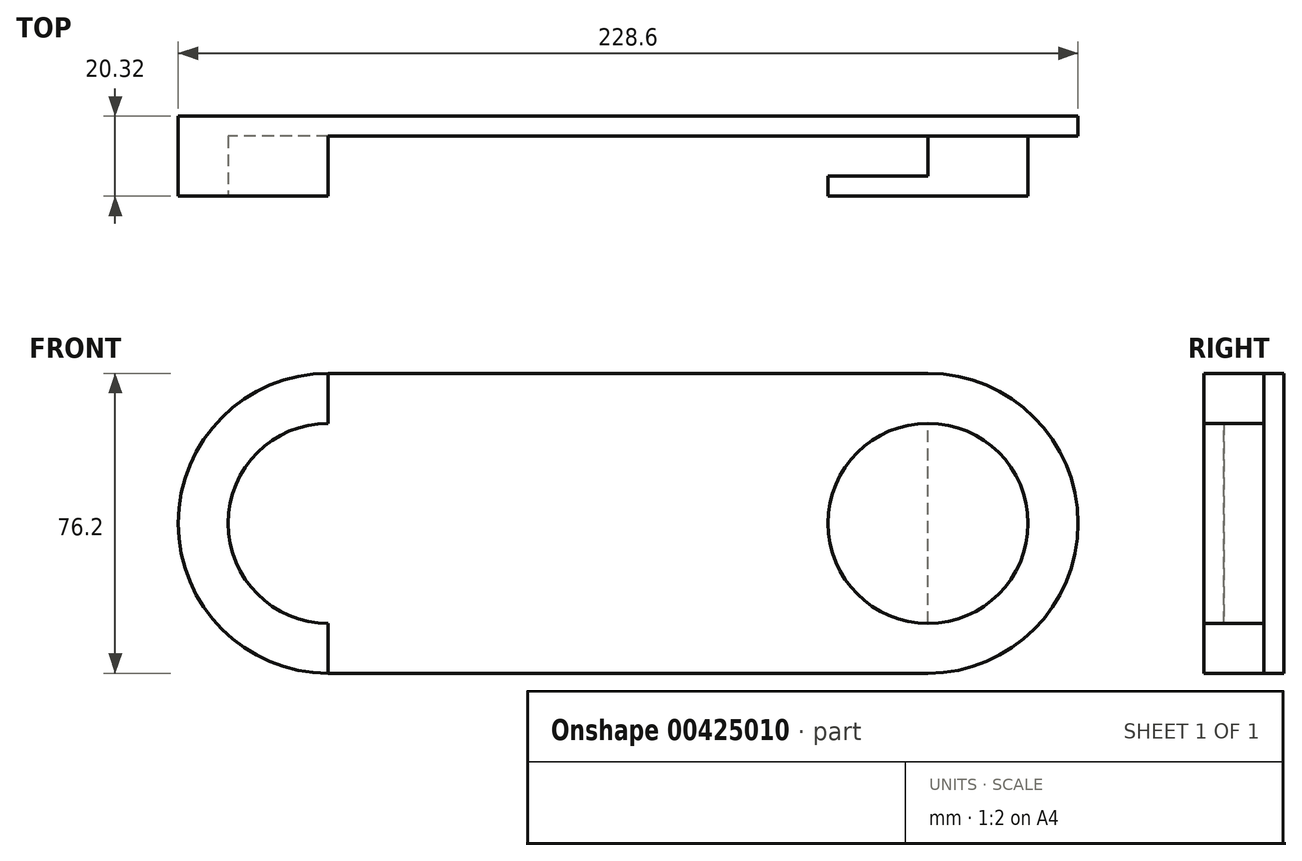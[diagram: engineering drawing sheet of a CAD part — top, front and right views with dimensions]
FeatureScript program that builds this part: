
annotation { "Feature Type Name" : "Feature", "Feature Type Description" : "" }
export const myFeature = defineFeature(function(context is Context, id is Id, definition is map)
    precondition{}
    {
        {
            var Q0;
            Q0=qCreatedBy(makeId("Front.planeOp"),FACE);
            var sketch = newSketch(context, id + "F0", { "sketchPlane" : qUnion([Q0])});
            skLineSegment(sketch, "E0.bottom", {"start": v(-47.72, 32.53) * mm, "end": v(104.68, 32.53) * mm});
            skLineSegment(sketch, "E0.top", {"start": v(-47.72, -43.67) * mm, "end": v(104.68, -43.67) * mm});
            skLineSegment(sketch, "E0.left", {"start": v(-47.72, 32.53) * mm, "end": v(-47.72, -43.67) * mm});
            skLineSegment(sketch, "E0.right", {"start": v(104.68, 32.53) * mm, "end": v(104.68, -43.67) * mm});
            skSolve(sketch);
        }
        {
            var Q0;
            Q0=makeQuery(id+"F0.imprint","IMPRINT",FACE,{"disambiguationData":[TD([[makeQuery(id+"F0.imprint","IMPRINT",EDGE,{"derivedFrom":sQuery(id+"F0.wireOp",EDGE,"E0.bottom")}),-1.0]])]});
            extrude(context, id + "F1", {"entities" : qUnion([Q0]), "depth" : 20.32 * mm});
        }
        {
            var Q0;
            Q0=makeQuery(id+"F1.opExtrude","SWEPT_FACE",FACE,{"disambiguationData":[OSD([sQuery(id+"F0.wireOp",EDGE,"E0.bottom")])]});
            var sketch = newSketch(context, id + "F2", { "sketchPlane" : qUnion([Q0])});
            skLineSegment(sketch, "E1.bottom", {"start": v(-9.62, -5.08) * mm, "end": v(66.58, -5.08) * mm});
            skLineSegment(sketch, "E1.top", {"start": v(-9.62, -15.24) * mm, "end": v(66.58, -15.24) * mm});
            skLineSegment(sketch, "E1.left", {"start": v(-9.62, -5.08) * mm, "end": v(-9.62, -15.24) * mm});
            skLineSegment(sketch, "E1.right", {"start": v(66.58, -5.08) * mm, "end": v(66.58, -15.24) * mm});
            skSolve(sketch);
        }
        {
            var Q0;
            Q0=makeQuery(id+"F2.imprint","IMPRINT",FACE,{"disambiguationData":[TD([[makeQuery(id+"F2.imprint","IMPRINT",EDGE,{"derivedFrom":sQuery(id+"F2.wireOp",EDGE,"E1.bottom")}),-1.0]])]});
            extrude(context, id + "F3", {"entities" : qUnion([Q0]), "operationType" : NewBodyOperationType.REMOVE, "oppositeDirection" : true, "depth" : 63.5 * mm});
        }
        {
            var Q0;
            Q0=makeQuery(id+"F1.opExtrude","CAP_FACE",FACE,{"disambiguationData":[OSD([sQuery(id+"F0.wireOp",EDGE,"E0.bottom"),sQuery(id+"F0.wireOp",EDGE,"E0.top"),sQuery(id+"F0.wireOp",EDGE,"E0.left"),sQuery(id+"F0.wireOp",EDGE,"E0.right")])],"isStart":false});
            var sketch = newSketch(context, id + "F4", { "sketchPlane" : qUnion([Q0])});
            skCircle(sketch, "E2", {"center": v(-47.72, -5.57) * mm, "radius": 38.1 * mm});
            skCircle(sketch, "E3", {"center": v(104.68, -5.57) * mm, "radius": 38.1 * mm});
            skSolve(sketch);
        }
        {
            var Q0;
            Q0=makeQuery(id+"F1.opExtrude","SWEPT_FACE",FACE,{"disambiguationData":[OSD([sQuery(id+"F0.wireOp",EDGE,"E0.left")])]});
            var sketch = newSketch(context, id + "F5", { "sketchPlane" : qUnion([Q0])});
            skLineSegment(sketch, "E4.bottom", {"start": v(5.08, -30.97) * mm, "end": v(15.24, -30.97) * mm});
            skLineSegment(sketch, "E4.top", {"start": v(5.08, 19.83) * mm, "end": v(15.24, 19.83) * mm});
            skLineSegment(sketch, "E4.left", {"start": v(5.08, -30.97) * mm, "end": v(5.08, 19.83) * mm});
            skLineSegment(sketch, "E4.right", {"start": v(15.24, -30.97) * mm, "end": v(15.24, 19.83) * mm});
            skSolve(sketch);
        }
        {
            var Q0;
            Q0=makeQuery(id+"F5.imprint","IMPRINT",FACE,{"disambiguationData":[TD([[makeQuery(id+"F5.imprint","IMPRINT",EDGE,{"derivedFrom":sQuery(id+"F5.wireOp",EDGE,"E4.bottom")}),1.0]])]});
            extrude(context, id + "F6", {"entities" : qUnion([Q0]), "operationType" : NewBodyOperationType.REMOVE, "oppositeDirection" : true, "depth" : 152.4 * mm});
        }
        {
            var Q0;
            {var subQ1=makeQuery(id+"F1.opExtrude","CAP_EDGE",EDGE,{"disambiguationData":[OSD([sQuery(id+"F0.wireOp",EDGE,"E0.left")])],"isStart":false});Q0=makeQuery(id+"F4.imprint","IMPRINT",FACE,{"disambiguationData":[TD([[makeQuery(id+"F4.imprint","IMPRINT",EDGE,{"derivedFrom":subQ1}),-1.0]])]});}
            var Q1;
            {var subQ1=makeQuery(id+"F1.opExtrude","CAP_EDGE",EDGE,{"disambiguationData":[OSD([sQuery(id+"F0.wireOp",EDGE,"E0.right")])],"isStart":false});Q1=makeQuery(id+"F4.imprint","IMPRINT",FACE,{"disambiguationData":[TD([[makeQuery(id+"F4.imprint","IMPRINT",EDGE,{"derivedFrom":subQ1}),1.0]])]});}
            extrude(context, id + "F7", {"entities" : qUnion([Q0, Q1]), "operationType" : NewBodyOperationType.ADD, "oppositeDirection" : true, "depth" : 20.32 * mm});
        }
        {
            var Q0;
            {var subQ0=sQuery(id+"F0.wireOp",EDGE,"E0.right");var subQ1=sQuery(id+"F0.wireOp",EDGE,"E0.left");Q0=makeQuery(id+"F7.boolean.opBoolean","MERGE",FACE,{"derivedFrom":[makeQuery(id+"F1.opExtrude","CAP_FACE",FACE,{"disambiguationData":[OSD([sQuery(id+"F0.wireOp",EDGE,"E0.bottom"),sQuery(id+"F0.wireOp",EDGE,"E0.top"),subQ1,subQ0])],"isStart":false}),makeQuery(id+"F7.opExtrude","CAP_FACE",FACE,{"disambiguationData":[OSD([subQ1,sQuery(id+"F4.wireOp",EDGE,"E2")])],"isStart":true}),makeQuery(id+"F7.opExtrude","CAP_FACE",FACE,{"disambiguationData":[OSD([subQ0,sQuery(id+"F4.wireOp",EDGE,"E3")])],"isStart":true})]});}
            var sketch = newSketch(context, id + "F8", { "sketchPlane" : qUnion([Q0])});
            skLineSegment(sketch, "E5", {"start": v(-47.72, 32.53) * mm, "end": v(-47.72, 19.83) * mm});
            skLineSegment(sketch, "E6", {"start": v(104.68, 32.53) * mm, "end": v(104.68, -43.67) * mm});
            skArc(sketch, "E7", {"start": v(-47.72, 19.83) * mm, "mid": v(-73.12, -5.57) * mm, "end": v(-47.72, -30.97) * mm});
            skCircle(sketch, "E8", {"center": v(104.68, -5.57) * mm, "radius": 25.4 * mm});
            skLineSegment(sketch, "E9.trimOffspring", {"start": v(-47.72, -30.97) * mm, "end": v(-47.72, -43.67) * mm});
            skLineSegment(sketch, "E10", {"start": v(-47.72, 19.83) * mm, "end": v(-47.72, -30.97) * mm});
            skCircle(sketch, "E11", {"center": v(-47.72, -5.57) * mm, "radius": 25.4 * mm});
            skSolve(sketch);
        }
        {
            var Q0;
            {var subQ0=sQuery(id+"F8.wireOp",EDGE,"E10");Q0=makeQuery(id+"F8.imprint","IMPRINT",FACE,{"disambiguationData":[TD([[makeQuery(id+"F8.imprint","IMPRINT",EDGE,{"derivedFrom":subQ0}),-1.0]])]});}
            var Q1;
            {var subQ0=sQuery(id+"F8.wireOp",EDGE,"E10");Q1=makeQuery(id+"F8.imprint","IMPRINT",FACE,{"disambiguationData":[TD([[makeQuery(id+"F8.imprint","IMPRINT",EDGE,{"derivedFrom":subQ0}),1.0]])]});}
            var Q2;
            {var subQ0=sQuery(id+"F8.wireOp",EDGE,"E8");var subQ1=sQuery(id+"F8.wireOp",EDGE,"E6");var subQ2=makeQuery(id+"F8.imprint","INTERSECT",VERTEX,{"disambiguationData":[OD(0.0)],"derivedFrom":[subQ1,subQ0]});Q2=makeQuery(id+"F8.imprint","IMPRINT",FACE,{"disambiguationData":[TD([[makeQuery(id+"F8.imprint","IMPRINT",EDGE,{"disambiguationData":[TD([[subQ2,-1.0]])],"derivedFrom":subQ1}),-1.0]])]});}
            var Q3;
            {var subQ0=sQuery(id+"F8.wireOp",EDGE,"E8");var subQ1=sQuery(id+"F8.wireOp",EDGE,"E6");var subQ2=makeQuery(id+"F8.imprint","INTERSECT",VERTEX,{"disambiguationData":[OD(0.0)],"derivedFrom":[subQ1,subQ0]});Q3=makeQuery(id+"F8.imprint","IMPRINT",FACE,{"disambiguationData":[TD([[makeQuery(id+"F8.imprint","IMPRINT",EDGE,{"disambiguationData":[TD([[subQ2,-1.0]])],"derivedFrom":subQ1}),1.0]])]});}
            extrude(context, id + "F9", {"entities" : qUnion([Q0, Q1, Q2, Q3]), "operationType" : NewBodyOperationType.REMOVE, "oppositeDirection" : true, "depth" : 15.24 * mm});
        }
        {
            var Q0;
            {var subQ0=sQuery(id+"F0.wireOp",EDGE,"E0.right");var subQ1=sQuery(id+"F0.wireOp",EDGE,"E0.left");Q0=makeQuery(id+"F7.boolean.opBoolean","MERGE",FACE,{"derivedFrom":[makeQuery(id+"F1.opExtrude","CAP_FACE",FACE,{"disambiguationData":[OSD([sQuery(id+"F0.wireOp",EDGE,"E0.bottom"),sQuery(id+"F0.wireOp",EDGE,"E0.top"),subQ1,subQ0])],"isStart":false}),makeQuery(id+"F7.opExtrude","CAP_FACE",FACE,{"disambiguationData":[OSD([subQ1,sQuery(id+"F4.wireOp",EDGE,"E2")])],"isStart":true}),makeQuery(id+"F7.opExtrude","CAP_FACE",FACE,{"disambiguationData":[OSD([subQ0,sQuery(id+"F4.wireOp",EDGE,"E3")])],"isStart":true})]});}
            var sketch = newSketch(context, id + "F10", { "sketchPlane" : qUnion([Q0])});
            skLineSegment(sketch, "E12.bottom", {"start": v(-9.62, 7.13) * mm, "end": v(66.58, 7.13) * mm});
            skLineSegment(sketch, "E12.top", {"start": v(-9.62, -18.27) * mm, "end": v(66.58, -18.27) * mm});
            skLineSegment(sketch, "E12.left", {"start": v(-9.62, 7.13) * mm, "end": v(-9.62, -18.27) * mm});
            skLineSegment(sketch, "E12.right", {"start": v(66.58, 7.13) * mm, "end": v(66.58, -18.27) * mm});
            skPoint(sketch, "E12.middle", {"position": v(28.48, -5.57) * mm});
            skPoint(sketch, "E13.start.orphan", {"position": v(-47.72, -5.57) * mm});
            skPoint(sketch, "E14.orphan", {"position": v(-47.72, 32.53) * mm});
            skPoint(sketch, "E15.end.orphan", {"position": v(-47.72, -43.67) * mm});
            skSolve(sketch);
        }
        {
            var Q0;
            Q0=makeQuery(id+"F10.imprint","IMPRINT",FACE,{"disambiguationData":[TD([[makeQuery(id+"F10.imprint","IMPRINT",EDGE,{"derivedFrom":sQuery(id+"F10.wireOp",EDGE,"E12.bottom")}),-1.0]])]});
            extrude(context, id + "F11", {"entities" : qUnion([Q0]), "operationType" : NewBodyOperationType.REMOVE, "oppositeDirection" : true, "depth" : 5.08 * mm});
        }
    });
